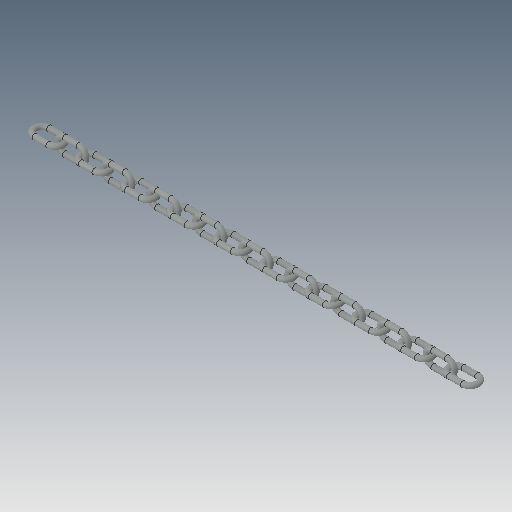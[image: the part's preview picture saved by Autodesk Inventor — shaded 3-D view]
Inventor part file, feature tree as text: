
AUTODESK INVENTOR PART (.ipt)
format: ipt  version: 2023.5 (Build 275446000, 446)  size: 764,928 bytes
history: native  units: in
note: dims shown in document units (in); Inventor stores cm internally (conversion verified against a paired STEP export)
features: other x17, sweep x2
ambient origin geometry x8: Origin, YZ Plane, XZ Plane, XY Plane, X Axis, Y Axis, Z Axis, Center Point
bodies: Solid1 (feature_tree), Solid2 (feature_tree), Solid3 (feature_tree), Solid4 (feature_tree), Solid5 (feature_tree), Solid6 (feature_tree), Solid7 (feature_tree), Solid8 (feature_tree), Solid9 (feature_tree), Solid10 (feature_tree), Solid11 (feature_tree), Solid12 (feature_tree), Solid13 (feature_tree), Solid14 (feature_tree), Solid15 (feature_tree), Solid16 (feature_tree), Solid17 (feature_tree), Solid18 (feature_tree), Solid19 (feature_tree)
feature tree (19):
  sweep  "Sweep1"
  sweep  "Sweep2"
  other  "LPattern1[1]"
  other  "LPattern1[2]"
  other  "LPattern1[3]"
  other  "LPattern1[4]"
  other  "LPattern1[5]"
  other  "LPattern1[6]"
  other  "LPattern1[7]"
  other  "LPattern1[8]"
  other  "LPattern1[9]"
  other  "LPattern1[10]"
  other  "LPattern1[11]"
  other  "LPattern1[12]"
  other  "LPattern1[13]"
  other  "LPattern1[14]"
  other  "LPattern1[15]"
  other  "LPattern1[16]"
  other  "LPattern3"
